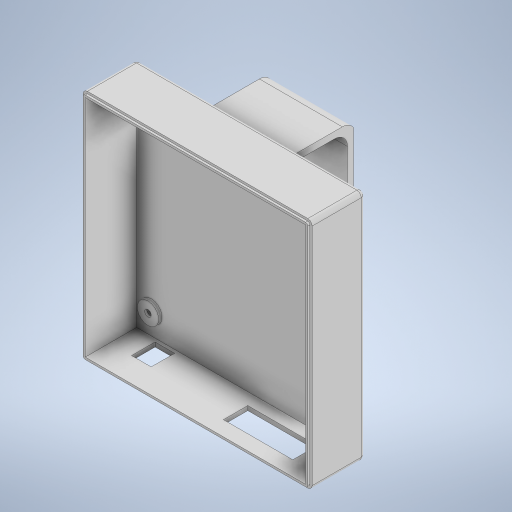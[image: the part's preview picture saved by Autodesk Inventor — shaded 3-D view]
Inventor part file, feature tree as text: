
AUTODESK INVENTOR PART (.ipt)
format: ipt  version: 2023 (Build 270158000, 158)  size: 501,760 bytes
history: native  units: mm
features: other x11, sketch x11, extrude x7, fillet x4, shell x1, split x1
ambient origin geometry x8: Origin, YZ Plane, XZ Plane, XY Plane, X Axis, Y Axis, Z Axis, Center Point
bodies: Body1 (feature_tree), Body2 (feature_tree), Body3 (feature_tree), Body4 (feature_tree)
feature tree (35):
  other  "Sólido1"
  sketch  "Boceto1"  dims[d0=95.0mm d1=95.0mm d2=86.4mm d3=86.7mm]
  extrude  "Extrusión1"  Depth=95.0mm
  fillet  "Empalme2"  Radius=86.4mm
  shell  "Vaciado6"  Thickness=86.7mm
  extrude  "Extrusión2"  Depth=4.8mm
  split  "Dividir1"
  other  "Soporte para fiador1"
  other  "Labio1"
  other  "Labio2"
  extrude  "Extrusión4"  Depth=34.5mm
  other  "Soporte para fiador3"
  other  "Soporte para fiador4"
  extrude  "Extrusión5"  Depth=41.5mm
  fillet  "Empalme4"  Radius=27.5mm
  extrude  "Extrusión9"  Depth=14.0mm
  fillet  "Empalme7"  Radius=10.0mm
  fillet  "Empalme8"  Radius=16.0mm
  extrude  "Extrusión10"  Depth=5.0mm
  extrude  "Extrusión11"  Depth=51.0mm TaperAngle=0.0deg
  sketch  "Boceto2"  dims[d4=4.55mm d5=4.8mm]
  sketch  "Boceto3"  dims[d6=4.8mm d7=34.5mm]
  sketch  "Boceto4"  dims[d8=31.8mm d9=41.5mm d10=27.5mm]
  other  "Sup1"
  sketch  "Boceto6"  dims[d11=9.0mm d12=14.0mm d13=10.0mm d14=16.0mm]
  sketch  "Boceto10"  dims[d15=5.0mm d16=5.0mm]
  sketch  "Boceto12"  dims[d17=5.0mm d18=51.0mm d19=0.0mm]
  sketch  "Boceto13"  dims[d26=2.0mm]
  other  "Sólido4"
  sketch  "Boceto20"  dims[d27=2.0mm]
  sketch  "Boceto21"  dims[d28=71.0mm]
  sketch  "Boceto22"  dims[d29=24.2mm d30=16.0mm d31=20.7mm d32=3.0mm d33=0.0mm d34=132.038888mm d35=25.5mm d36=0.0mm d37=0.0mm d41=75.0mm d42=31.0mm d43=27.5mm d44=73.0mm d45=0.0mm d46=5.0mm d47=5.8mm d48=1.0mm d49=0.0mm d50=5.8mm d51=1.0mm d52=3.0mm d53=0.436332mm d54=0.436332mm d55=0.436332mm d56=0.436332mm d57=90.0deg d58=20.0mm d60=2.0mm d61=2.0mm d62=10.0mm d63=0.0mm d64=1.745329mm d65=0.436332mm d66=0.0mm d67=0.0mm d68=0.0mm d69=360.0deg d70=1.0mm d71=1.0mm d72=0.0mm d73=0.0mm d74=0.0mm d75=0.0mm d76=1.0mm d77=1.0mm d78=0.0mm d79=0.0mm d80=0.0mm d81=0.0mm d82=1.5mm d83=10.8mm d84=5.5mm d85=11.2mm d86=3.0mm d87=0.0mm d113=0.0mm d114=3.5mm d126=20.0mm d128=2.0mm d129=2.0mm d130=2.0mm d131=0.0mm d132=1.745329mm d133=0.436332mm d134=0.0mm d135=0.0mm d136=0.0mm d137=360.0deg d143=5.9mm d144=2.0mm d145=0.0mm d146=5.9mm d147=1.0mm d148=3.0mm d149=0.436332mm d150=0.436332mm d151=0.436332mm d152=0.436332mm d153=90.0deg d154=0.0mm d155=44.0mm d156=5.8mm d157=2.8mm d158=9.5mm d159=0.349066mm d160=0.174533mm d161=20.0mm d163=2.0mm d164=2.0mm d165=2.0mm d166=0.0mm d167=1.745329mm d168=0.436332mm d169=0.0mm d170=0.0mm d171=0.0mm d172=360.0deg d173=38.0mm d174=3.0mm d175=33.5mm d176=5.0mm d177=30.0mm d178=0.0mm d183=6.0mm d203=2.8mm d204=36.0mm d205=0.0mm d206=3.0mm d207=6.0mm d208=0.0mm d209=0.0mm d210=3.0mm d211=0.0mm]
  other  "SuperficieBarrido1"
  other  "Sólido2"
  other  "Sólido3"
